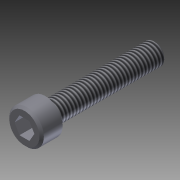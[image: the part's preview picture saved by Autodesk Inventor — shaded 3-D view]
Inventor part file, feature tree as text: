
AUTODESK INVENTOR PART (.ipt)
format: ipt  version: 2011 (Build 150239000, 239)  size: 103,936 bytes
history: native  units: in
note: dims shown in document units (in); Inventor stores cm internally (conversion verified against a paired STEP export)
features: extrude x3, sketch x3, chamfer x2, thread x1
ambient origin geometry x8: Origin, YZ Plane, XZ Plane, XY Plane, X Axis, Y Axis, Z Axis, Center Point
bodies: Solid1 (feature_tree)
feature tree (9):
  extrude  "Extrusion1"  Depth=0.19in TaperAngle=0.0deg
  extrude  "Extrusion2"  Depth=1.0in TaperAngle=0.0deg
  extrude  "Extrusion3"  Depth=0.125in TaperAngle=0.0deg
  thread  "Thread1"  [1 undecoded]
  chamfer  "Chamfer1"  Distance=0.02in Angle=45.0deg
  chamfer  "Chamfer2"  Distance=0.02in Angle=45.0deg
  sketch  "Sketch1"  dims[d0=0.312in d1=0.19in d2=0.0in]
  sketch  "Sketch2"  dims[d3=0.19in d4=1.0in d5=0.0in]
  sketch  "Sketch3"  dims[d6=0.1562in d7=0.125in d8=0.0in d9=1.0in d10=0.0in d11=0.02in d12=0.125in d13=45.0deg d14=0.02in d15=0.125in d16=45.0deg]
note: 1 required parameter value undecoded (feature->parameter linkage not recoverable at this tier; creation-order binding heuristic only, values carry confidence <= 0.55)
